# Revit family: Shower_Arm-Rainshower-Grohe-26635_Series
name_source: partatom
category: Plumbing Fixtures
revit_build: Autodesk Revit 2018 (Build: 20170223_1515(x64)
units: mm (PartAtom-declared; Revit-internal decimal feet)

## family parameters
Cut with Voids When Loaded = No
Host = Face
OmniClass Number = 23.45.05.14.17
OmniClass Title = Showers
Part Type = Normal
Room Calculation Point = No
Round Connector Dimension = Use Diameter
Shared = Yes

## types (5) — shared parameters
Assembly Code = D2010700
CW Connection = Yes
CWFU = 3
Default Elevation = 0"
Description = RainShower Wall Union, 1/2
HW Connection = Yes
HWFU = 3
Height = 1 15/16"
Installation Type = Wall-mounted
Length = 2 1/2"
Manufacturer = Grohe
Price = Prices may vary. Please consult Manufacturer Representative for most up-to-date price list.
Product Documentation Link = https://americanstandard.box.com
Product Page URL = https://www.grohe.us
Region = North America
URL = https://www.grohe.us
Vent Connection = No
WFU = 4
Warranty Information = Limited Lifetime Warranty
Waste Connection = No
Width = 1 15/16"

## per-type parameters (varying)
| type | Body Material | Material |
| 26635000 | Metal-Grohe-000-Starlight Chrome | Metal-Grohe-000-Starlight Chrome |
| 26635A00 | Metal-Grohe-A00-Hard Graphite | Metal-Grohe-A00-Hard Graphite |
| 26635BE0 | Metal-Grohe-BE0-Polished Nickel Infinity Finish | Metal-Grohe-BE0-Polished Nickel Infinity Finish |
| 26635EN0 | Metal-Grohe-EN0-Brushed Nickel Infinity Finish | Metal-Grohe-EN0-Brushed Nickel Infinity Finish |
| 26635GN0 | Metal-Grohe-GN0-Brushed Cool Sunrise | Metal-Grohe-GN0-Brushed Cool Sunrise |

note: column(s) folded — value = type name in every type: Model

## geometry (parser evidence)
native form markers: Sweep x3
no freeform markers — native parametric forms only
